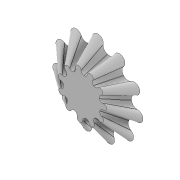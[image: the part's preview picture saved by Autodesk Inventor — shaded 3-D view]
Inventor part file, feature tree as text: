
AUTODESK INVENTOR PART (.ipt)
format: ipt  version: 2020 (Build 240168000, 168)  size: 617,472 bytes
history: native  units: in
note: dims shown in document units (in); Inventor stores cm internally (conversion verified against a paired STEP export)
features: sketch x2, plane x1, loft x1
ambient origin geometry x8: Origin, YZ Plane, XZ Plane, XY Plane, X Axis, Y Axis, Z Axis, Center Point
bodies: Body1 (feature_tree)
feature tree (4):
  sketch  "Sketch1"  dims[d0=0.1969in d1=0.1575in]
  plane  "Work Plane1"
  loft  "Loft2"
  sketch  "Sketch6"  dims[d2=0.0866in d3=0.0827in d4=0.0827in d5=0.0827in d6=4.3307in d8=360.0deg d10=0.1181in d31=0.1181in d32=4.3307in d34=360.0deg d36=0.0in d37=90.0deg d38=0.0in d39=90.0deg]
